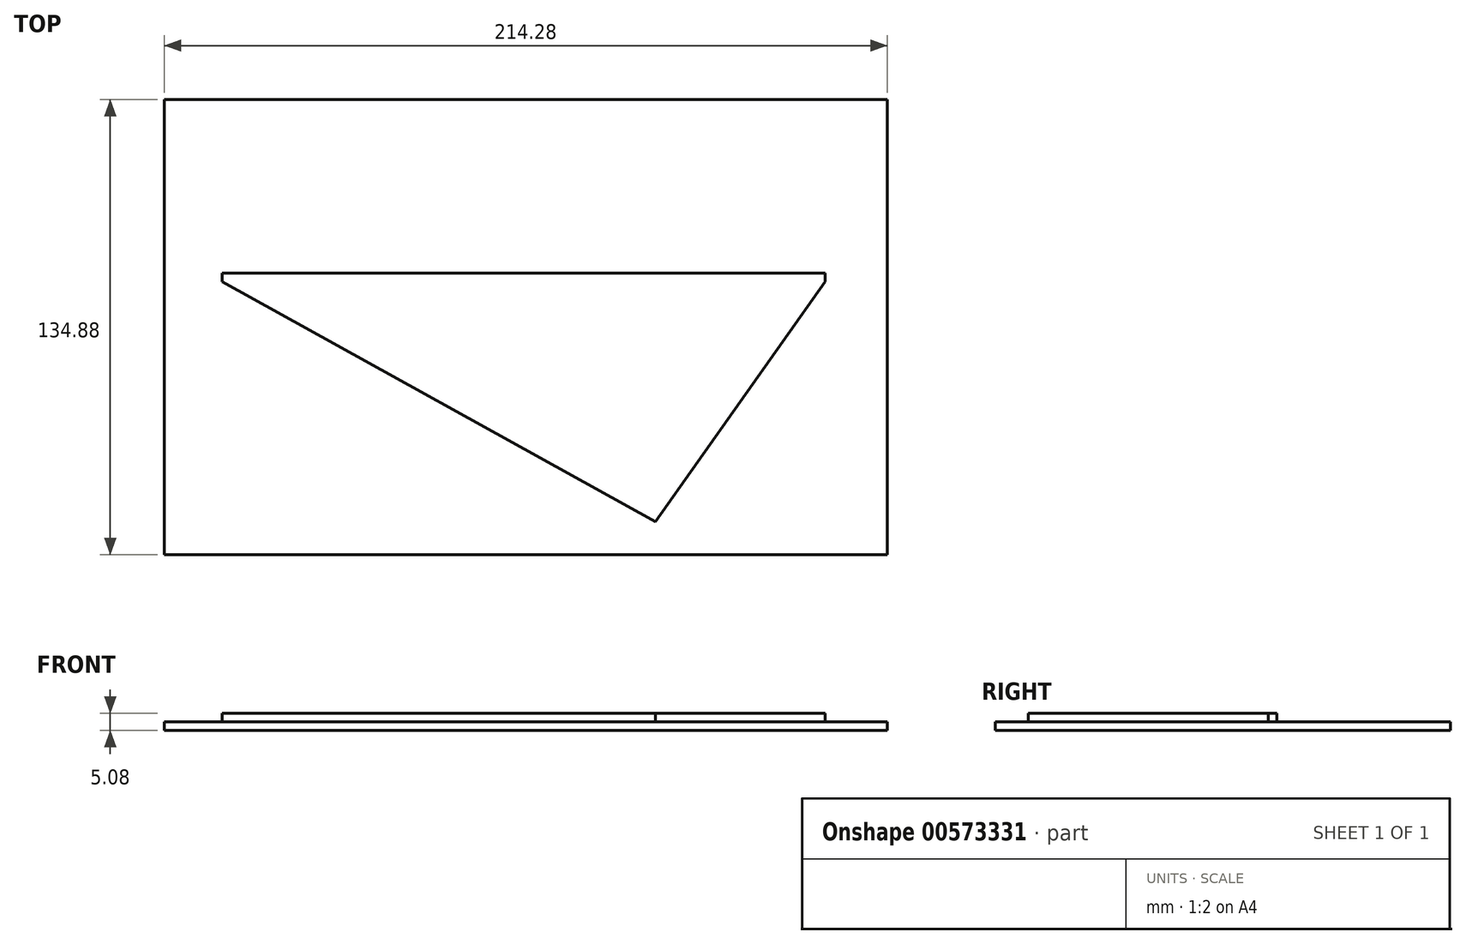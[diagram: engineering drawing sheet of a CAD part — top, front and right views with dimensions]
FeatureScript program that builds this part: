
annotation { "Feature Type Name" : "Feature", "Feature Type Description" : "" }
export const myFeature = defineFeature(function(context is Context, id is Id, definition is map)
    precondition{}
    {
        {
            var Q0;
            Q0=qCreatedBy(makeId("Top.planeOp"),FACE);
            var sketch = newSketch(context, id + "F0", { "sketchPlane" : qUnion([Q0])});
            skLineSegment(sketch, "E0.bottom", {"start": v(-107.14, 65.14) * mm, "end": v(107.14, 65.14) * mm});
            skLineSegment(sketch, "E0.top", {"start": v(-107.14, -69.74) * mm, "end": v(107.14, -69.74) * mm});
            skLineSegment(sketch, "E0.left", {"start": v(-107.14, 65.14) * mm, "end": v(-107.14, -69.74) * mm});
            skLineSegment(sketch, "E0.right", {"start": v(107.14, 65.14) * mm, "end": v(107.14, -69.74) * mm});
            skPoint(sketch, "E0.middle", {"position": v(0, -2.3) * mm});
            skLineSegment(sketch, "E1", {"start": v(88.75, 11.19) * mm, "end": v(38.47, -59.93) * mm});
            skLineSegment(sketch, "E2", {"start": v(38.47, -59.93) * mm, "end": v(-89.97, 11.19) * mm});
            skLineSegment(sketch, "E3", {"start": v(-89.97, 11.19) * mm, "end": v(-89.97, 13.73) * mm});
            skLineSegment(sketch, "E4", {"start": v(-89.97, 13.73) * mm, "end": v(88.75, 13.73) * mm});
            skLineSegment(sketch, "E5", {"start": v(88.75, 13.73) * mm, "end": v(88.75, 11.19) * mm});
            skSolve(sketch);
        }
        {
            var Q0;
            Q0=makeQuery(id+"F0.imprint","IMPRINT",FACE,{"disambiguationData":[TD([[makeQuery(id+"F0.imprint","IMPRINT",EDGE,{"derivedFrom":sQuery(id+"F0.wireOp",EDGE,"E0.bottom")}),-1.0]])]});
            extrude(context, id + "F1", {"entities" : qUnion([Q0]), "depth" : 2.54 * mm, "offsetDistance" : 25.4 * mm});
        }
        {
            var Q0;
            Q0=makeQuery(id+"F0.imprint","IMPRINT",FACE,{"disambiguationData":[TD([[makeQuery(id+"F0.imprint","IMPRINT",EDGE,{"derivedFrom":sQuery(id+"F0.wireOp",EDGE,"E1")}),-1.0]])]});
            extrude(context, id + "F2", {"entities" : qUnion([Q0]), "operationType" : NewBodyOperationType.ADD, "depth" : 5.08 * mm, "offsetDistance" : 25.4 * mm});
        }
    });
